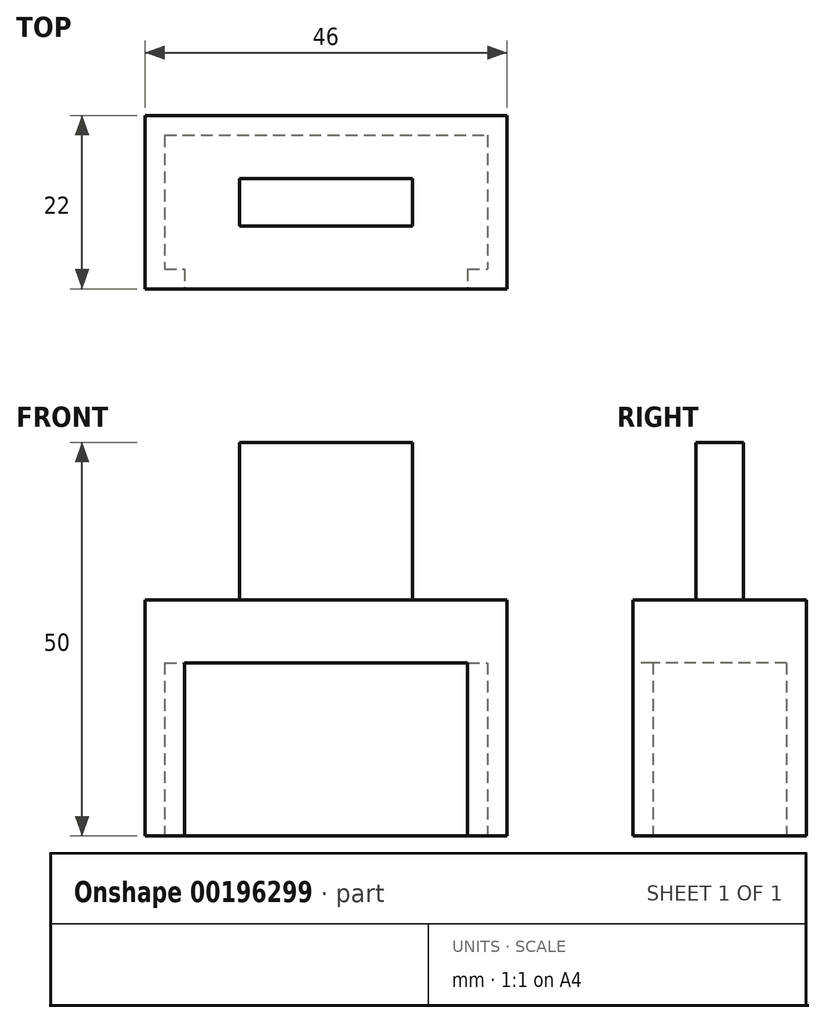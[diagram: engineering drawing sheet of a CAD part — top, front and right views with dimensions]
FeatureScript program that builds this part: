
annotation { "Feature Type Name" : "Feature", "Feature Type Description" : "" }
export const myFeature = defineFeature(function(context is Context, id is Id, definition is map)
    precondition{}
    {
        {
            var Q0;
            Q0=qCreatedBy(makeId("Top.planeOp"),FACE);
            var sketch = newSketch(context, id + "F0", { "sketchPlane" : qUnion([Q0])});
            skLineSegment(sketch, "E0.bottom", {"start": v(-23, 11) * mm, "end": v(23, 11) * mm});
            skLineSegment(sketch, "E0.top", {"start": v(-23, -11) * mm, "end": v(23, -11) * mm});
            skLineSegment(sketch, "E0.left", {"start": v(-23, 11) * mm, "end": v(-23, -11) * mm});
            skLineSegment(sketch, "E0.right", {"start": v(23, 11) * mm, "end": v(23, -11) * mm});
            skPoint(sketch, "E0.middle", {"position": v(0, 0) * mm});
            skSolve(sketch);
        }
        {
            var Q0;
            Q0=makeQuery(id+"F0.imprint","IMPRINT",FACE,{"disambiguationData":[TD([[makeQuery(id+"F0.imprint","IMPRINT",EDGE,{"derivedFrom":sQuery(id+"F0.wireOp",EDGE,"E0.bottom")}),-1.0]])]});
            extrude(context, id + "F1", {"entities" : qUnion([Q0]), "depth" : 30 * mm});
        }
        {
            var Q0;
            Q0=makeQuery(id+"F1.opExtrude","CAP_FACE",FACE,{"disambiguationData":[OSD([sQuery(id+"F0.wireOp",EDGE,"E0.bottom"),sQuery(id+"F0.wireOp",EDGE,"E0.top"),sQuery(id+"F0.wireOp",EDGE,"E0.left"),sQuery(id+"F0.wireOp",EDGE,"E0.right")])],"isStart":true});
            var sketch = newSketch(context, id + "F2", { "sketchPlane" : qUnion([Q0])});
            skLineSegment(sketch, "E1.bottom", {"start": v(-20.5, -8.5) * mm, "end": v(20.5, -8.5) * mm});
            skLineSegment(sketch, "E1.top", {"start": v(-20.5, 8.5) * mm, "end": v(20.5, 8.5) * mm});
            skLineSegment(sketch, "E1.left", {"start": v(-20.5, -8.5) * mm, "end": v(-20.5, 8.5) * mm});
            skLineSegment(sketch, "E1.right", {"start": v(20.5, -8.5) * mm, "end": v(20.5, 8.5) * mm});
            skPoint(sketch, "E1.middle", {"position": v(0, 0) * mm});
            skSolve(sketch);
        }
        {
            var Q0;
            Q0=makeQuery(id+"F2.imprint","IMPRINT",FACE,{"disambiguationData":[TD([[makeQuery(id+"F2.imprint","IMPRINT",EDGE,{"derivedFrom":sQuery(id+"F2.wireOp",EDGE,"E1.bottom")}),1.0]])]});
            extrude(context, id + "F3", {"entities" : qUnion([Q0]), "operationType" : NewBodyOperationType.REMOVE, "oppositeDirection" : true, "depth" : 22 * mm});
        }
        {
            var Q0;
            Q0=makeQuery(id+"F1.opExtrude","SWEPT_FACE",FACE,{"disambiguationData":[OSD([sQuery(id+"F0.wireOp",EDGE,"E0.top")])]});
            var sketch = newSketch(context, id + "F4", { "sketchPlane" : qUnion([Q0])});
            skLineSegment(sketch, "E2.bottom", {"start": v(18, 0) * mm, "end": v(-18, 0) * mm});
            skLineSegment(sketch, "E2.top", {"start": v(18, 22) * mm, "end": v(-18, 22) * mm});
            skLineSegment(sketch, "E2.left", {"start": v(18, 0) * mm, "end": v(18, 22) * mm});
            skLineSegment(sketch, "E2.right", {"start": v(-18, 0) * mm, "end": v(-18, 22) * mm});
            skSolve(sketch);
        }
        {
            var Q0;
            Q0=makeQuery(id+"F4.imprint","IMPRINT",FACE,{"disambiguationData":[TD([[makeQuery(id+"F4.imprint","IMPRINT",EDGE,{"derivedFrom":sQuery(id+"F4.wireOp",EDGE,"E2.bottom")}),1.0]])]});
            extrude(context, id + "F5", {"entities" : qUnion([Q0]), "operationType" : NewBodyOperationType.REMOVE, "oppositeDirection" : true, "depth" : 4 * mm});
        }
        {
            var Q0;
            Q0=makeQuery(id+"F1.opExtrude","CAP_FACE",FACE,{"disambiguationData":[OSD([sQuery(id+"F0.wireOp",EDGE,"E0.bottom"),sQuery(id+"F0.wireOp",EDGE,"E0.top"),sQuery(id+"F0.wireOp",EDGE,"E0.left"),sQuery(id+"F0.wireOp",EDGE,"E0.right")])],"isStart":false});
            var sketch = newSketch(context, id + "F6", { "sketchPlane" : qUnion([Q0])});
            skLineSegment(sketch, "E3.bottom", {"start": v(11, -3) * mm, "end": v(-11, -3) * mm});
            skLineSegment(sketch, "E3.top", {"start": v(11, 3) * mm, "end": v(-11, 3) * mm});
            skLineSegment(sketch, "E3.left", {"start": v(11, -3) * mm, "end": v(11, 3) * mm});
            skLineSegment(sketch, "E3.right", {"start": v(-11, -3) * mm, "end": v(-11, 3) * mm});
            skPoint(sketch, "E3.middle", {"position": v(0, 0) * mm});
            skSolve(sketch);
        }
        {
            var Q0;
            Q0=makeQuery(id+"F6.imprint","IMPRINT",FACE,{"disambiguationData":[TD([[makeQuery(id+"F6.imprint","IMPRINT",EDGE,{"derivedFrom":sQuery(id+"F6.wireOp",EDGE,"E3.bottom")}),-1.0]])]});
            extrude(context, id + "F7", {"entities" : qUnion([Q0]), "operationType" : NewBodyOperationType.ADD, "depth" : 20 * mm});
        }
    });
